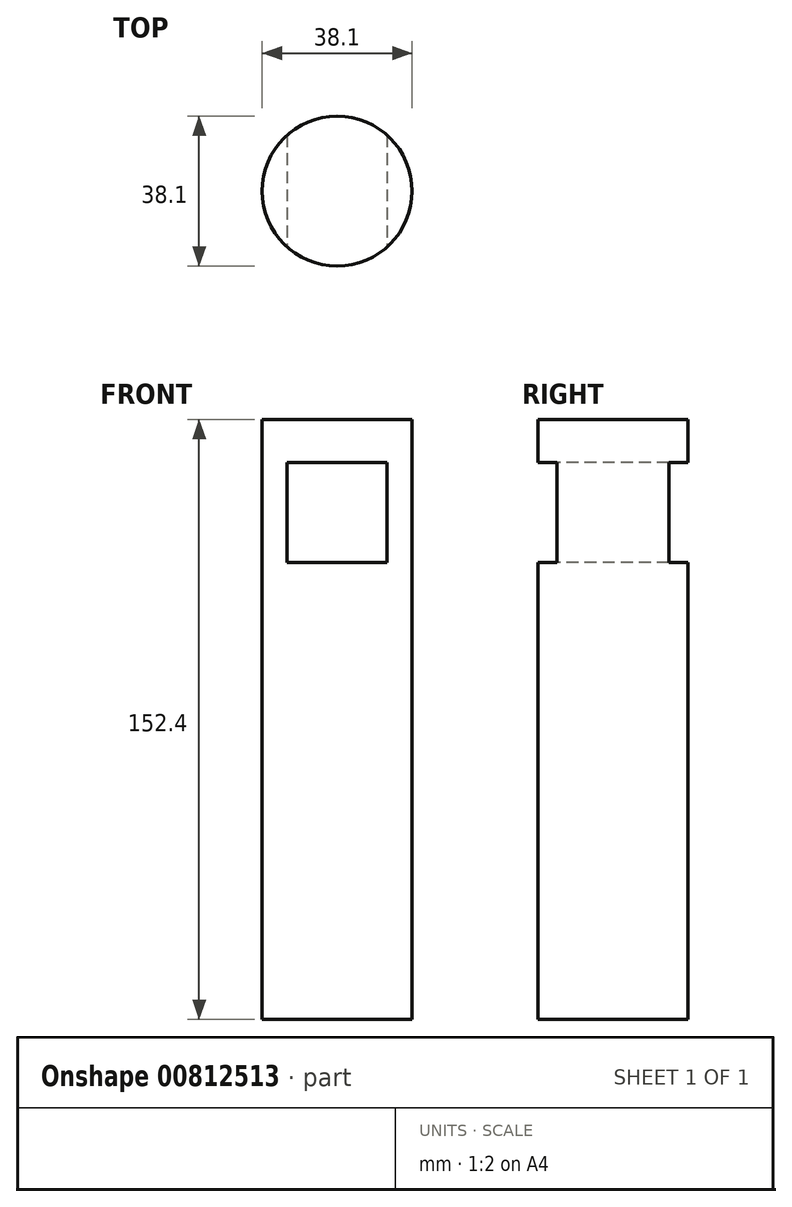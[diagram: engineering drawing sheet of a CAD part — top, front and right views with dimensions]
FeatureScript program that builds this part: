
annotation { "Feature Type Name" : "Feature", "Feature Type Description" : "" }
export const myFeature = defineFeature(function(context is Context, id is Id, definition is map)
    precondition{}
    {
        {
            var Q0;
            Q0=qCreatedBy(makeId("Top.planeOp"),FACE);
            var sketch = newSketch(context, id + "F0", { "sketchPlane" : qUnion([Q0])});
            skCircle(sketch, "E0", {"center": v(0, 0) * mm, "radius": 19.05 * mm});
            skSolve(sketch);
        }
        {
            var Q0;
            Q0=qCreatedBy(makeId("Front.planeOp"),FACE);
            var sketch = newSketch(context, id + "F1", { "sketchPlane" : qUnion([Q0])});
            skLineSegment(sketch, "E1.bottom", {"start": v(12.7, 65.24) * mm, "end": v(-12.7, 65.24) * mm});
            skLineSegment(sketch, "E1.top", {"start": v(12.7, 39.84) * mm, "end": v(-12.7, 39.84) * mm});
            skLineSegment(sketch, "E1.left", {"start": v(12.7, 65.24) * mm, "end": v(12.7, 39.84) * mm});
            skLineSegment(sketch, "E1.right", {"start": v(-12.7, 65.24) * mm, "end": v(-12.7, 39.84) * mm});
            skSolve(sketch);
        }
        {
            var Q0;
            Q0=makeQuery(id+"F0.imprint","IMPRINT",FACE,{"disambiguationData":[TD([[makeQuery(id+"F0.imprint","IMPRINT",EDGE,{"derivedFrom":sQuery(id+"F0.wireOp",EDGE,"E0")}),1.0]])]});
            extrude(context, id + "F2", {"entities" : qUnion([Q0]), "endBound" : BoundingType.SYMMETRIC, "depth" : 152.4 * mm, "offsetDistance" : 25.4 * mm});
        }
        {
            var Q0;
            Q0=makeQuery(id+"F1.imprint","IMPRINT",FACE,{"disambiguationData":[TD([[makeQuery(id+"F1.imprint","IMPRINT",EDGE,{"derivedFrom":sQuery(id+"F1.wireOp",EDGE,"E1.bottom")}),1.0]])]});
            extrude(context, id + "F3", {"entities" : qUnion([Q0]), "operationType" : NewBodyOperationType.REMOVE, "endBound" : BoundingType.SYMMETRIC, "oppositeDirection" : true, "depth" : 50.8 * mm, "offsetDistance" : 25.4 * mm});
        }
    });
